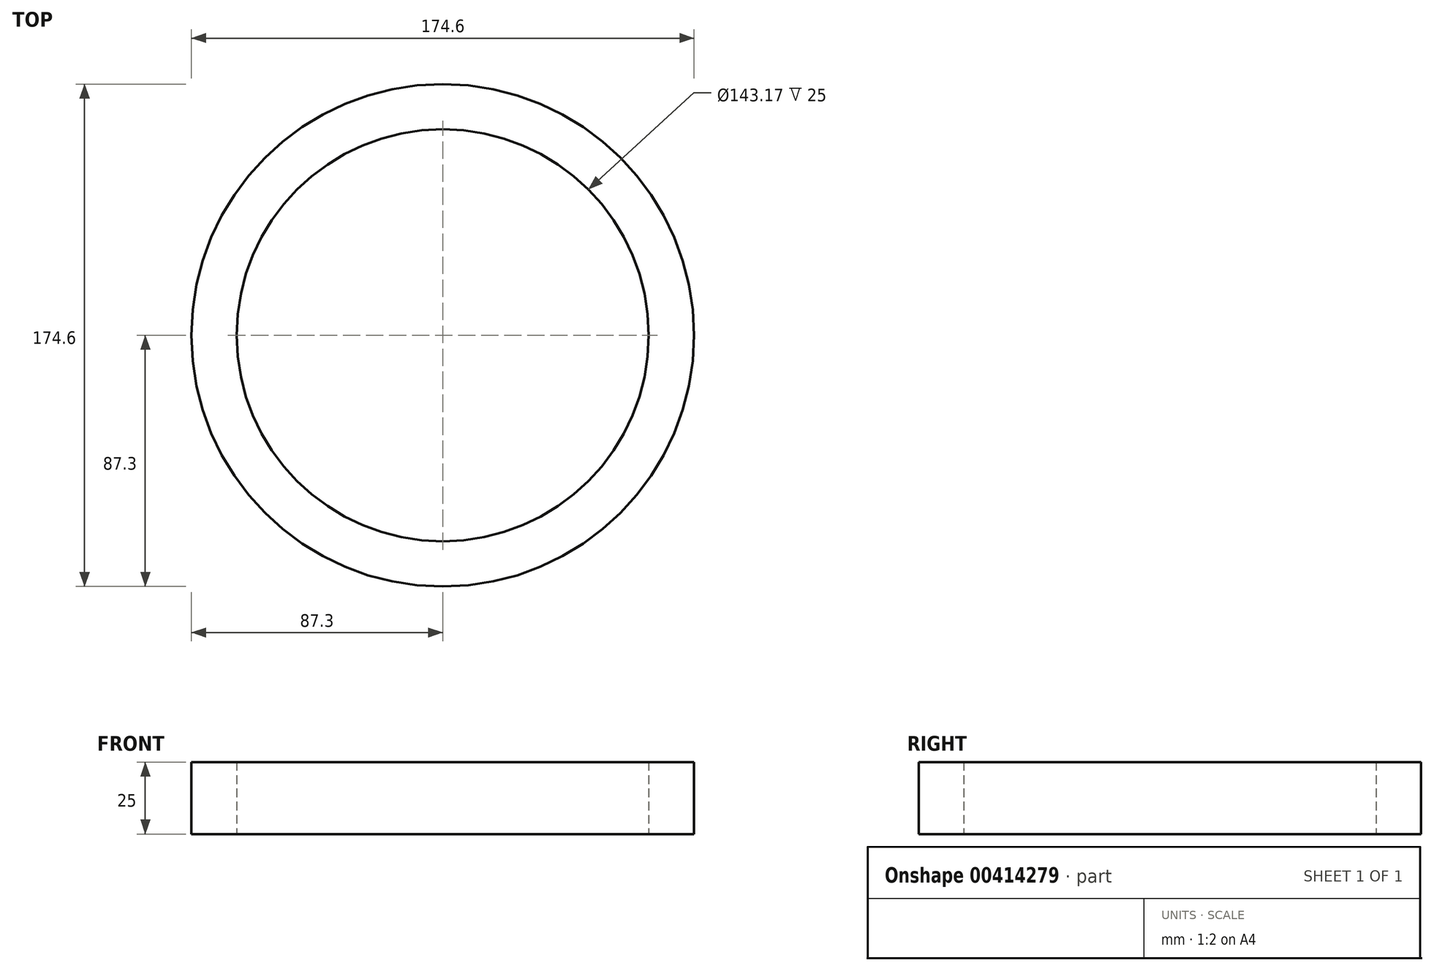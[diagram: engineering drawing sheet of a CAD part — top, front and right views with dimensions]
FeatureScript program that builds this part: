
annotation { "Feature Type Name" : "Feature", "Feature Type Description" : "" }
export const myFeature = defineFeature(function(context is Context, id is Id, definition is map)
    precondition{}
    {
        {
            var Q0;
            Q0=qCreatedBy(makeId("Top.planeOp"),FACE);
            var sketch = newSketch(context, id + "F0", { "sketchPlane" : qUnion([Q0])});
            skCircle(sketch, "E0", {"center": v(0, 0) * mm, "radius": 87.3 * mm});
            skSolve(sketch);
        }
        {
            var Q0;
            Q0=makeQuery(id+"F0.imprint","IMPRINT",FACE,{"disambiguationData":[TD([[makeQuery(id+"F0.imprint","IMPRINT",EDGE,{"derivedFrom":sQuery(id+"F0.wireOp",EDGE,"E0")}),1.0]])]});
            var Q1;
            Q1 = qSketchRegion(id + "F0", true);
            extrude(context, id + "F1", {"entities" : qUnion([Q0, Q1]), "depth" : 25 * mm});
        }
        {
            var Q0;
            Q0=makeQuery(id+"F1.opExtrude","CAP_FACE",FACE,{"disambiguationData":[OSD([sQuery(id+"F0.wireOp",EDGE,"E0")])],"isStart":true});
            var sketch = newSketch(context, id + "F2", { "sketchPlane" : qUnion([Q0])});
            skCircle(sketch, "E1", {"center": v(0, 0) * mm, "radius": 71.58 * mm});
            skSolve(sketch);
        }
        {
            var Q0;
            Q0=makeQuery(id+"F2.imprint","IMPRINT",FACE,{"disambiguationData":[TD([[makeQuery(id+"F2.imprint","IMPRINT",EDGE,{"derivedFrom":sQuery(id+"F2.wireOp",EDGE,"E1")}),1.0]])]});
            extrude(context, id + "F3", {"entities" : qUnion([Q0]), "operationType" : NewBodyOperationType.REMOVE, "oppositeDirection" : true, "depth" : 25 * mm});
        }
    });
